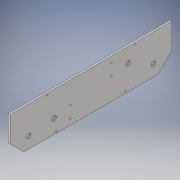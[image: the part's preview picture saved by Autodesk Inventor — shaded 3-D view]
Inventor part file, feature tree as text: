
AUTODESK INVENTOR PART (.ipt)
format: ipt  version: 2017 (Build 210142000, 142)  size: 173,568 bytes
history: native  units: in
note: dims shown in document units (in); Inventor stores cm internally (conversion verified against a paired STEP export)
features: sketch x4, projected_geometry x3, extrude x2, chamfer x2, hole x2
ambient origin geometry x8: Origin, YZ Plane, XZ Plane, XY Plane, X Axis, Y Axis, Z Axis, Center Point
bodies: Solid1 (feature_tree)
feature tree (13):
  extrude  "Extrusion1"  Depth=17.5in
  chamfer  "Chamfer1"  Distance=2.0in
  chamfer  "Chamfer2"  Distance=0.1875in
  extrude  "Extrusion2"  Depth=0.1875in TaperAngle=45.0deg
  hole  "Hole1"  [1 undecoded]
  hole  "Hole2"  [1 undecoded]
  sketch  "Sketch1"  dims[d0=4.25in d1=17.5in]
  sketch  "Sketch2"  dims[d2=0.501in]
  projected_geometry  "Projected Loop1"
  sketch  "Sketch6"  dims[d3=1.25in]
  projected_geometry  "Projected Loop5"
  sketch  "Sketch7"  dims[d4=2.0in d5=2.0in d6=0.1875in d7=0.0in d8=1.5in d9=0.125in d10=45.0deg d11=1.5in d12=0.125in d13=45.0deg d14=0.501in d15=4.75in d17=0.501in d19=4.75in d20=1.0in d21=0.0in d22=6.517in d23=0.125in d24=0.603in d25=0.125in d26=0.63in d27=6.517in d28=0.125in d29=0.603in d30=6.517in d31=0.125in d32=0.63in d33=6.517in d78=1.535in d79=1.535in d80=1.26in d81=1.776in d82=1.776in d83=0.63in d84=1.776in d85=1.776in d86=1.26in d87=0.63in d88=0.15in d89=0.75in d90=0.375in d91=0.25in d92=0.5635in d93=1.0in d94=0.8108in d95=0.175in d96=0.175in d97=0.175in d98=0.175in d99=4.0in d100=4.0in d101=5.0in d102=5.0in d103=0.15in d104=0.75in d105=0.375in d106=0.25in d107=0.5635in d108=1.0in d109=0.8108in]
  projected_geometry  "Projected Loop6"
note: 2 required parameter values undecoded (feature->parameter linkage not recoverable at this tier; creation-order binding heuristic only, values carry confidence <= 0.55)
